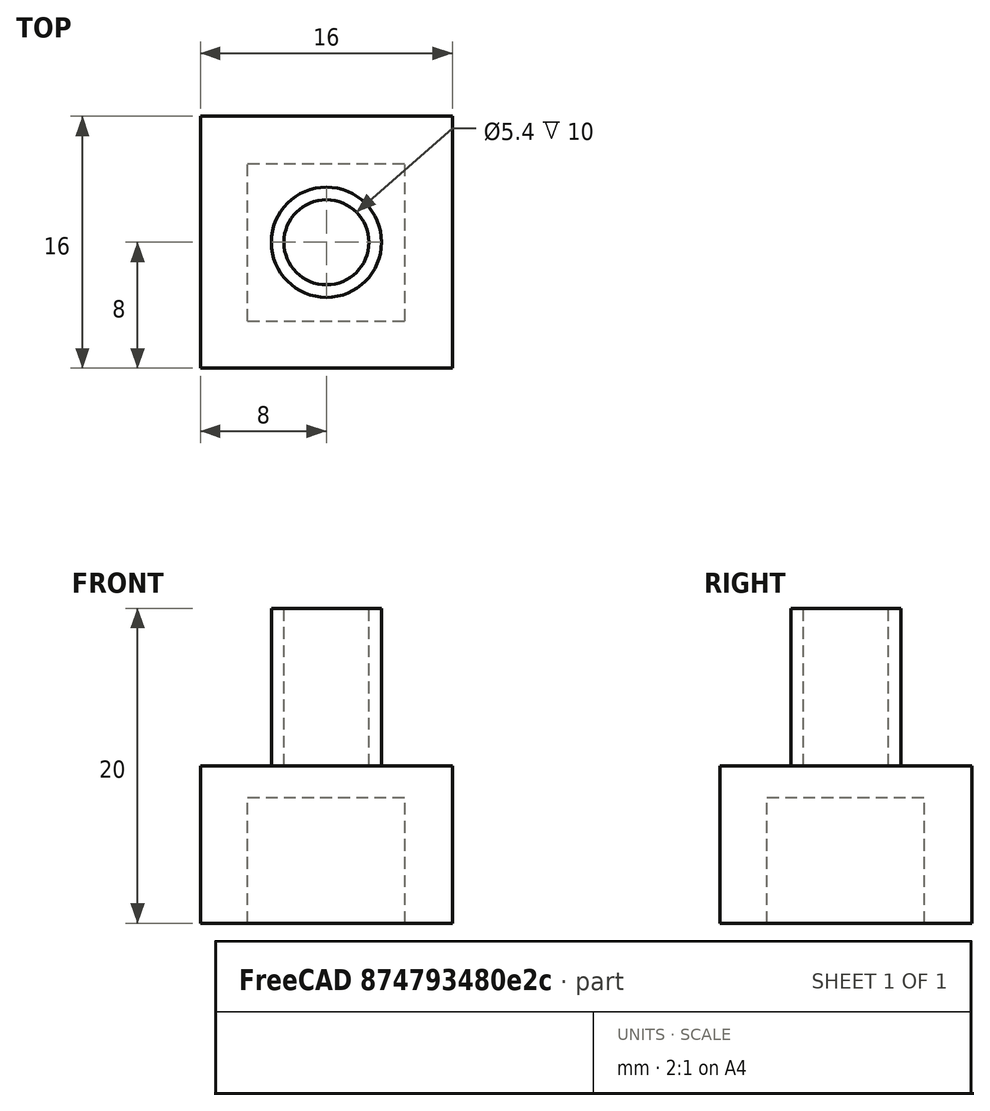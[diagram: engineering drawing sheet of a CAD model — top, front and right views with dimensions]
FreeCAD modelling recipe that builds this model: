
FCSTD DOCUMENT  (FreeCAD 0.18.3R)
Label: cylinder_shell
License: All rights reserved
LicenseURL: http://en.wikipedia.org/wiki/All_rights_reserved
objects: Part::Box×2, Part::Cylinder×2, Part::Cut×2, Part::Fuse×1
note: 7 computed .brp shape members not serialized (recipe doc carries the construction recipe); baked Part::Feature solids carry a one-line shape summary decoded from their .brp

FEATURE [Part::Box] Box  label="Cube"
  AttacherType = Attacher::AttachEngine3D
  Height = 10
  Length = 16
  Placement = pos=(-8,-8,0) rot=(0,0,1;0rad)
  Width = 16
FEATURE [Part::Cylinder] Cylinder
  Angle = 360
  AttacherType = Attacher::AttachEngine3D
  Height = 10
  Placement = pos=(0,0,10) rot=(0,0,1;0rad)
  Radius = 2.7
FEATURE [Part::Cylinder] Cylinder001
  Angle = 360
  AttacherType = Attacher::AttachEngine3D
  Height = 10
  Placement = pos=(0,0,10) rot=(0,0,1;0rad)
  Radius = 3.5
FEATURE [Part::Cut] Cut
  Base = -> Cylinder001
  Tool = -> Cylinder
FEATURE [Part::Fuse] Fusion
  Base = -> Box
  Tool = -> Cut
FEATURE [Part::Box] Box001  label="Cube001"
  AttacherType = Attacher::AttachEngine3D
  Height = 8
  Length = 10
  Placement = pos=(-5,-5,0) rot=(0,0,1;0rad)
  Width = 10
FEATURE [Part::Cut] Cut001
  Base = -> Fusion
  Tool = -> Box001
